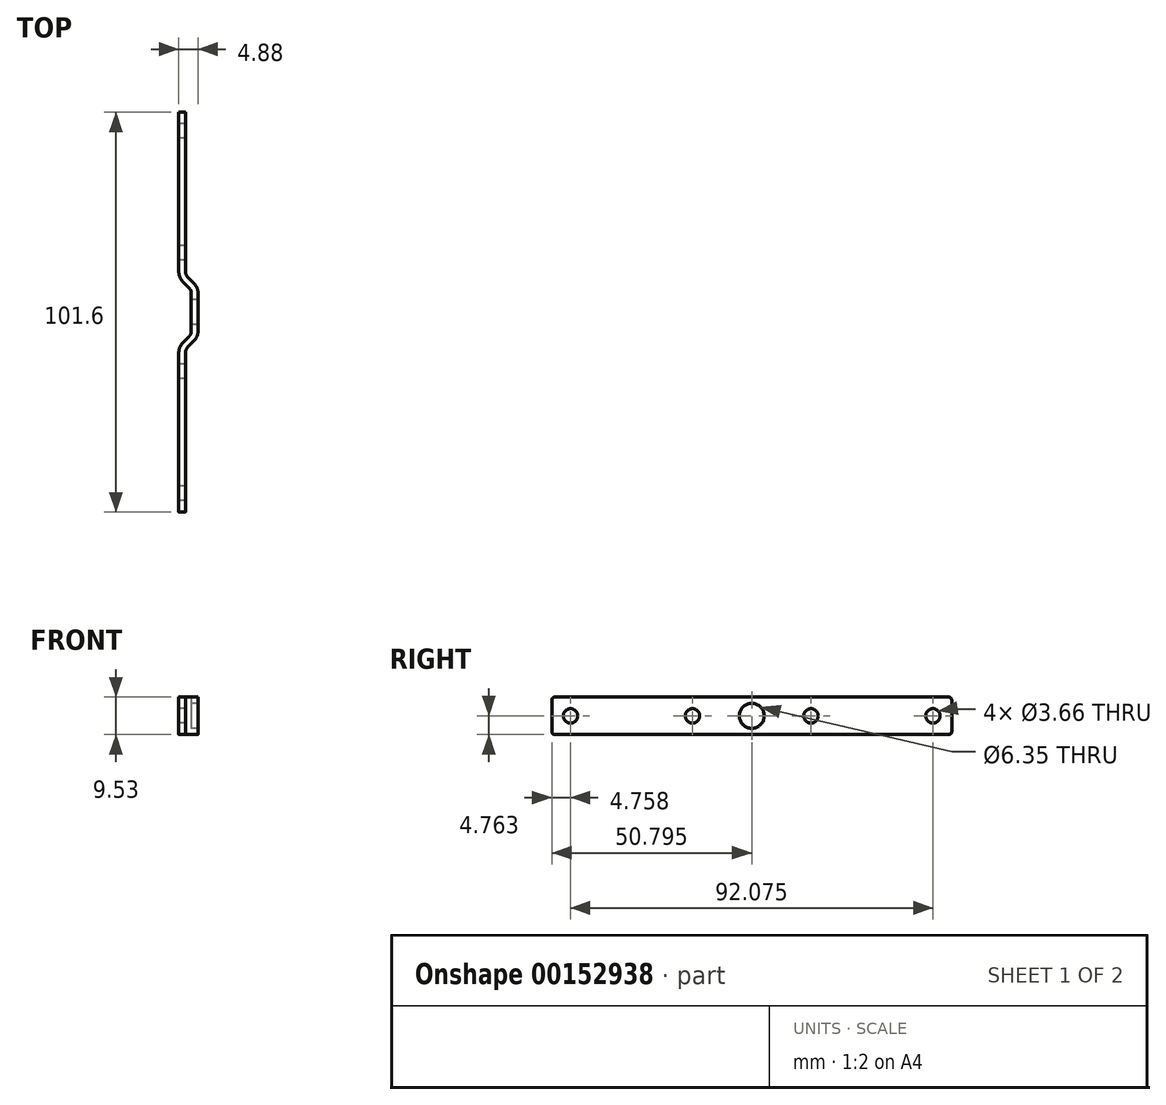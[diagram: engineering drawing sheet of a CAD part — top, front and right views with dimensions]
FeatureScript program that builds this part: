
annotation { "Feature Type Name" : "Feature", "Feature Type Description" : "" }
export const myFeature = defineFeature(function(context is Context, id is Id, definition is map)
    precondition{}
    {
        {
            var Q0;
            Q0=qCreatedBy(makeId("Top.planeOp"),FACE);
            var sketch = newSketch(context, id + "F0", { "sketchPlane" : qUnion([Q0])});
            skArc(sketch, "E0", {"start": v(0, 0) * mm, "mid": v(0.43, 0.64) * mm, "end": v(0.58, 1.4) * mm});
            skLineSegment(sketch, "E1", {"start": v(0, 0) * mm, "end": v(-1.51, -1.51) * mm});
            skArc(sketch, "E2", {"start": v(-1.51, -1.51) * mm, "mid": v(-2.31, -2.71) * mm, "end": v(-2.6, -4.12) * mm});
            skLineSegment(sketch, "E3", {"start": v(-2.6, -4.12) * mm, "end": v(-2.6, 16.45) * mm, "construction": true});
            skLineSegment(sketch, "E4", {"start": v(0.58, 1.4) * mm, "end": v(0.58, 10.93) * mm});
            skLineSegment(sketch, "E5", {"start": v(0.58, 6.17) * mm, "end": v(-2.6, 6.17) * mm, "construction": true});
            skLineSegment(sketch, "E6", {"start": v(-0.76, -0.76) * mm, "end": v(0.45, -1.96) * mm, "construction": true});
            skLineSegment(sketch, "E7", {"start": v(-0.3, -2.72) * mm, "end": v(1.2, -1.2) * mm});
            skArc(sketch, "E8", {"start": v(1.2, -1.2) * mm, "mid": v(2, -0.01) * mm, "end": v(2.3, 1.4) * mm});
            skArc(sketch, "E9", {"start": v(-0.3, -2.72) * mm, "mid": v(-0.73, -3.36) * mm, "end": v(-0.88, -4.12) * mm});
            skLineSegment(sketch, "E10", {"start": v(-2.6, -4.12) * mm, "end": v(-0.88, -4.12) * mm, "construction": true});
            skLineSegment(sketch, "E11", {"start": v(0.58, 1.4) * mm, "end": v(2.3, 1.4) * mm, "construction": true});
            skLineSegment(sketch, "E12", {"start": v(2.3, 1.4) * mm, "end": v(2.3, 10.93) * mm});
            skLineSegment(sketch, "E13", {"start": v(-2.6, -4.12) * mm, "end": v(-2.6, -44.63) * mm});
            skLineSegment(sketch, "E14", {"start": v(-0.88, -4.12) * mm, "end": v(-0.88, -44.63) * mm});
            skLineSegment(sketch, "E15", {"start": v(-0.88, -44.63) * mm, "end": v(-2.6, -44.63) * mm});
            skArc(sketch, "E16", {"start": v(-2.6, 16.45) * mm, "mid": v(-2.31, 15.04) * mm, "end": v(-1.51, 13.84) * mm});
            skArc(sketch, "E17", {"start": v(0.58, 10.93) * mm, "mid": v(0.43, 11.69) * mm, "end": v(0, 12.33) * mm});
            skLineSegment(sketch, "E18", {"start": v(-1.51, 13.84) * mm, "end": v(0, 12.33) * mm});
            skLineSegment(sketch, "E19", {"start": v(0.58, 10.93) * mm, "end": v(2.3, 10.93) * mm, "construction": true});
            skArc(sketch, "E20", {"start": v(2.3, 10.93) * mm, "mid": v(2, 12.34) * mm, "end": v(1.2, 13.54) * mm});
            skArc(sketch, "E21", {"start": v(-0.88, 16.45) * mm, "mid": v(-0.73, 15.7) * mm, "end": v(-0.3, 15.05) * mm});
            skLineSegment(sketch, "E22", {"start": v(1.2, 13.54) * mm, "end": v(-0.3, 15.05) * mm});
            skLineSegment(sketch, "E23", {"start": v(-2.6, 16.45) * mm, "end": v(-0.88, 16.45) * mm, "construction": true});
            skLineSegment(sketch, "E24", {"start": v(-2.6, 16.45) * mm, "end": v(-2.6, 56.97) * mm});
            skLineSegment(sketch, "E25", {"start": v(-2.6, 56.97) * mm, "end": v(-0.88, 56.97) * mm});
            skLineSegment(sketch, "E26", {"start": v(-0.88, 56.97) * mm, "end": v(-0.88, 16.45) * mm});
            skSolve(sketch);
        }
        {
            var Q0;
            Q0 = qSketchRegion(id + "F0", true);
            extrude(context, id + "F1", {"entities" : qUnion([Q0]), "depth" : 9.52 * mm});
        }
        {
            var Q0;
            {var subQ0=sQuery(id+"F0.wireOp",EDGE,"E24");Q0=makeQuery(id+"FBPYhQcztcHPAAm_1.boolean.opBoolean","MERGE",FACE,{"derivedFrom":[makeQuery(id+"F1.opExtrude","SWEPT_FACE",FACE,{"disambiguationData":[OSD([subQ0])]}),makeQuery(id+"FBPYhQcztcHPAAm_1.opExtrude","SWEPT_FACE",FACE,{"disambiguationData":[OSD([subQ0])]})]});}
            var sketch = newSketch(context, id + "F2", { "sketchPlane" : qUnion([Q0])});
            skLineSegment(sketch, "E27.bottom", {"start": v(-56.97, 4.76) * mm, "end": v(-52.2, 4.76) * mm, "construction": true});
            skLineSegment(sketch, "E27.top", {"start": v(-56.97, 9.53) * mm, "end": v(-52.2, 9.53) * mm, "construction": true});
            skLineSegment(sketch, "E27.left", {"start": v(-56.97, 4.76) * mm, "end": v(-56.97, 9.53) * mm, "construction": true});
            skLineSegment(sketch, "E27.right", {"start": v(-52.2, 4.76) * mm, "end": v(-52.2, 9.53) * mm, "construction": true});
            skLineSegment(sketch, "E28.bottom", {"start": v(44.63, 4.76) * mm, "end": v(39.87, 4.76) * mm, "construction": true});
            skLineSegment(sketch, "E28.top", {"start": v(44.63, 9.53) * mm, "end": v(39.87, 9.53) * mm, "construction": true});
            skLineSegment(sketch, "E28.left", {"start": v(44.63, 4.76) * mm, "end": v(44.63, 9.53) * mm, "construction": true});
            skLineSegment(sketch, "E28.right", {"start": v(39.87, 4.76) * mm, "end": v(39.87, 9.52) * mm, "construction": true});
            skLineSegment(sketch, "E29", {"start": v(-16.45, 4.76) * mm, "end": v(-21.22, 4.76) * mm, "construction": true});
            skLineSegment(sketch, "E30", {"start": v(4.12, 4.76) * mm, "end": v(8.89, 4.76) * mm, "construction": true});
            skCircle(sketch, "E31", {"center": v(-52.2, 4.76) * mm, "radius": 1.83 * mm});
            skCircle(sketch, "E32", {"center": v(-21.22, 4.76) * mm, "radius": 1.83 * mm});
            skCircle(sketch, "E33", {"center": v(8.89, 4.76) * mm, "radius": 1.83 * mm});
            skCircle(sketch, "E34", {"center": v(39.87, 4.76) * mm, "radius": 1.83 * mm});
            skLineSegment(sketch, "E35", {"start": v(-16.45, 4.76) * mm, "end": v(4.12, 4.76) * mm, "construction": true});
            skCircle(sketch, "E36", {"center": v(-6.17, 4.76) * mm, "radius": 3.18 * mm});
            skSolve(sketch);
        }
        {
            var Q0;
            Q0 = qSketchRegion(id + "F2", true);
            var Q1;
            Q1=makeQuery(id+"F1.opExtrude","SWEPT_FACE",FACE,{"disambiguationData":[OSD([sQuery(id+"F0.wireOp",EDGE,"E12")])]});
            extrude(context, id + "F3", {"entities" : qUnion([Q0]), "operationType" : NewBodyOperationType.REMOVE, "endBound" : BoundingType.UP_TO_SURFACE, "oppositeDirection" : true, "endBoundEntityFace" : qUnion([Q1]), "depth" : 25.4 * mm});
        }
        {
            var Q0;
            Q0=makeQuery(id+"F1.opExtrude","CAP_EDGE",EDGE,{"disambiguationData":[OSD([sQuery(id+"F0.wireOp",EDGE,"E25")])],"isStart":false});
            var Q1;
            Q1=makeQuery(id+"F1.opExtrude","CAP_EDGE",EDGE,{"disambiguationData":[OSD([sQuery(id+"F0.wireOp",EDGE,"E25")])],"isStart":true});
            var Q2;
            Q2=makeQuery(id+"F1.opExtrude","CAP_EDGE",EDGE,{"disambiguationData":[OSD([sQuery(id+"F0.wireOp",EDGE,"E15")])],"isStart":false});
            var Q3;
            Q3=makeQuery(id+"F1.opExtrude","CAP_EDGE",EDGE,{"disambiguationData":[OSD([sQuery(id+"F0.wireOp",EDGE,"E15")])],"isStart":true});
            fillet(context, id + "F4", {"entities" : qUnion([Q0, Q1, Q2, Q3]), "radius" : 0.76 * mm, "tangentPropagation" : true, "allowEdgeOverflow" : false});
        }
    });
